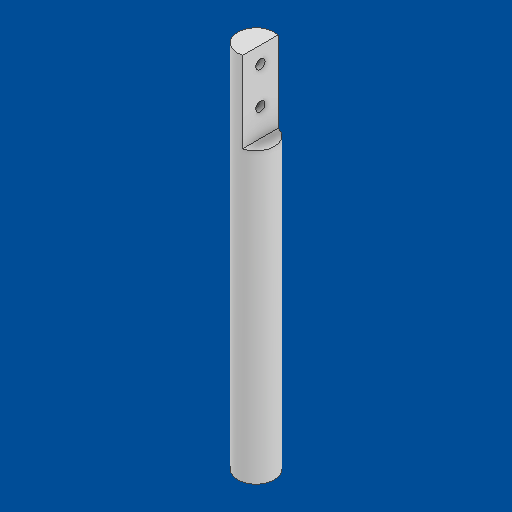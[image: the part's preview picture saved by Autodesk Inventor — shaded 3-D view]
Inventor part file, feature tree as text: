
AUTODESK INVENTOR PART (.ipt)
format: ipt  version: 2025 (Build 290162000, 162)  size: 669,696 bytes
history: native  units: mm
features: other x10, direct_edit x9, sketch x3, plane x2, split x2, hole x2, delete_face x1, extrude x1, move_body x1
ambient origin geometry x8: Origin, YZ Plane, XZ Plane, XY Plane, X Axis, Y Axis, Z Axis, Center Point
bodies: Solid1 (feature_tree), Solid2 (feature_tree), Solid3 (feature_tree), Solid4 (feature_tree), Solid5 (feature_tree), Solid6 (feature_tree)
feature tree (31):
  plane  "Work Plane1"
  split  "Split1"
  delete_face  "Delete Face1"
  extrude  "Extrusion1"  Depth=25.4mm TaperAngle=0.0deg
  direct_edit  "Direct Edit1"
  plane  "Work Plane3"
  split  "Split2"
  direct_edit  "Direct Edit2"
  direct_edit  "Direct Edit3"
  direct_edit  "Direct Edit4"
  direct_edit  "Direct Edit5"
  direct_edit  "Direct Edit6"
  hole  "Hole1"  [1 undecoded]
  direct_edit  "Direct Edit7"
  hole  "Hole2"  [1 undecoded]
  direct_edit  "Direct Edit8"
  direct_edit  "Direct Edit9"
  sketch  "Sketch1"  dims[d0=25.0mm d1=25.4mm d2=0.0mm]
  sketch  "Sketch2"  dims[d3=-1.905mm d5=-1.27mm]
  sketch  "Sketch3"  dims[d6=99.844mm d7=-0.114mm d8=-0.019mm d9=-0.981mm d10=0.5mm d11=2.0mm d12=2.0mm d13=3.242mm d14=10.0mm d15=4.0mm d16=2.0mm d17=90.0deg d18=8.0mm d19=20.594885mm d20=1.25mm d21=3.0mm d22=4.917mm d23=40.0mm d24=4.0mm d25=2.0mm d26=90.0deg d27=40.0mm d28=20.594885mm d29=0.5mm d30=0.0mm d31=0.0mm d32=1.0mm]
  other  "13073-001-1-solid1"
  other  "21110-001-1-solid1"
  other  "Size1"
  other  "Size2"
  other  "Size3"
  other  "Size4"
  other  "Size5"
  other  "Size6"
  other  "Size7"
  other  "Size8"
  move_body  "Move1"
note: 2 required parameter values undecoded (feature->parameter linkage not recoverable at this tier; creation-order binding heuristic only, values carry confidence <= 0.55)
